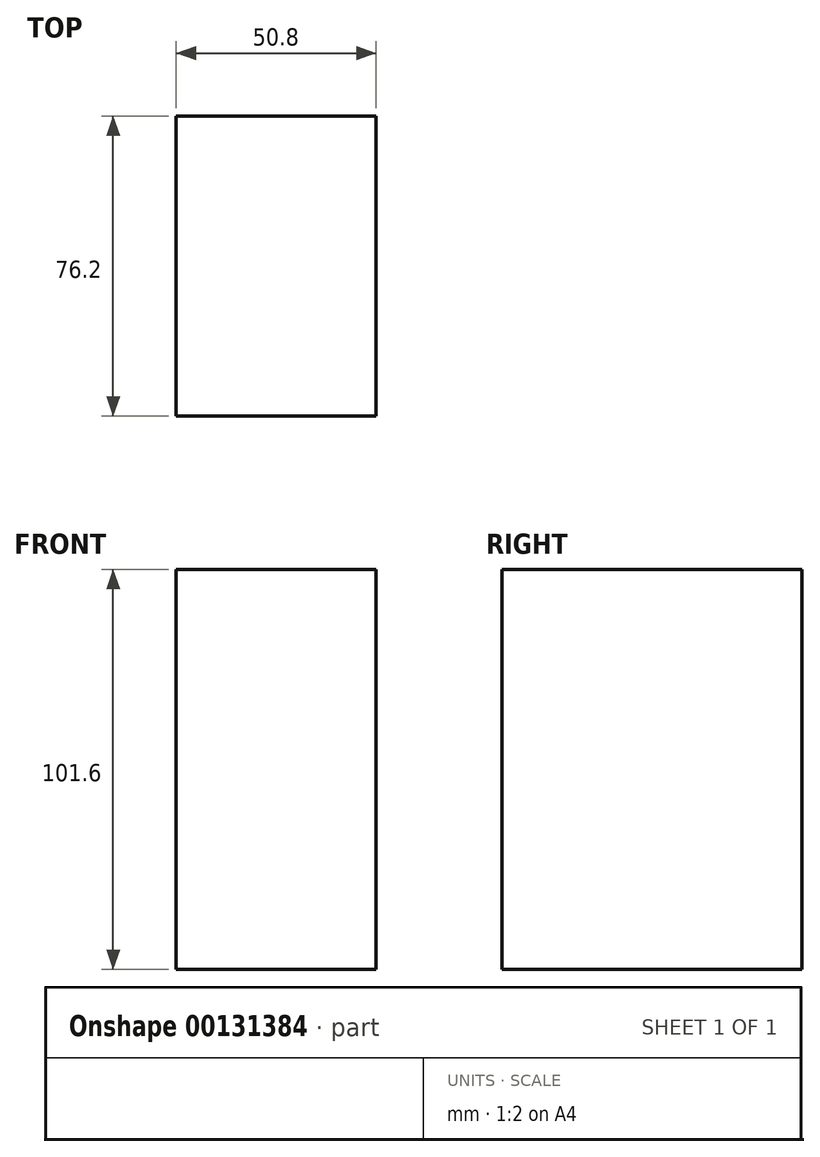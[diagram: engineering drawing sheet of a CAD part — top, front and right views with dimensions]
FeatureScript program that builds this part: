
annotation { "Feature Type Name" : "Feature", "Feature Type Description" : "" }
export const myFeature = defineFeature(function(context is Context, id is Id, definition is map)
    precondition{}
    {
        {
            var Q0;
            Q0=qCreatedBy(makeId("Front.planeOp"),FACE);
            var sketch = newSketch(context, id + "F0", { "sketchPlane" : qUnion([Q0])});
            skLineSegment(sketch, "E0.bottom", {"start": v(-25.4, -50.8) * mm, "end": v(25.4, -50.8) * mm});
            skLineSegment(sketch, "E0.top", {"start": v(-25.4, 50.8) * mm, "end": v(25.4, 50.8) * mm});
            skLineSegment(sketch, "E0.left", {"start": v(-25.4, -50.8) * mm, "end": v(-25.4, 50.8) * mm});
            skLineSegment(sketch, "E0.right", {"start": v(25.4, -50.8) * mm, "end": v(25.4, 50.8) * mm});
            skPoint(sketch, "E0.middle", {"position": v(0, 0) * mm});
            skSolve(sketch);
        }
        {
            var Q0;
            Q0=makeQuery(id+"F0.imprint","IMPRINT",FACE,{"disambiguationData":[TD([[makeQuery(id+"F0.imprint","IMPRINT",EDGE,{"derivedFrom":sQuery(id+"F0.wireOp",EDGE,"E0.bottom")}),1.0]])]});
            extrude(context, id + "F1", {"entities" : qUnion([Q0]), "endBound" : BoundingType.SYMMETRIC, "depth" : 76.2 * mm});
        }
    });
